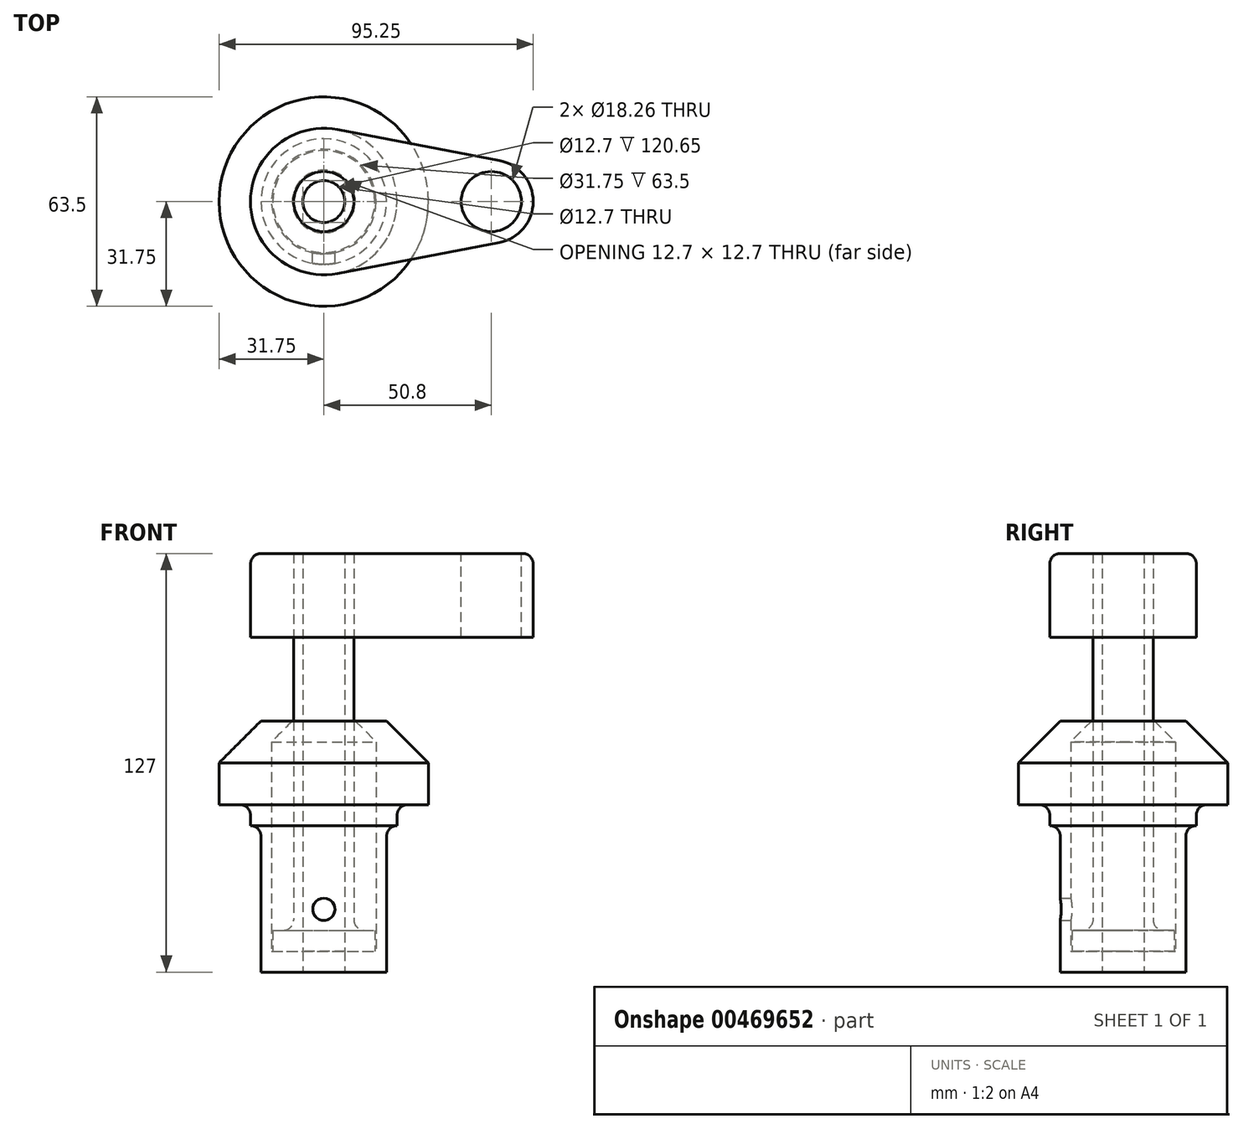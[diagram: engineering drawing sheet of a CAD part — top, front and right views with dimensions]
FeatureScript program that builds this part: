
annotation { "Feature Type Name" : "Feature", "Feature Type Description" : "" }
export const myFeature = defineFeature(function(context is Context, id is Id, definition is map)
    precondition{}
    {
        {
            var Q0;
            Q0=qCreatedBy(makeId("Front.planeOp"),FACE);
            var sketch = newSketch(context, id + "F0", { "sketchPlane" : qUnion([Q0])});
            skLineSegment(sketch, "E0", {"start": v(0, 0) * mm, "end": v(0, 76.2) * mm});
            skLineSegment(sketch, "E1", {"start": v(0, 76.2) * mm, "end": v(19.05, 76.2) * mm});
            skLineSegment(sketch, "E2", {"start": v(19.05, 76.2) * mm, "end": v(31.75, 63.5) * mm});
            skLineSegment(sketch, "E3", {"start": v(31.75, 63.5) * mm, "end": v(31.75, 50.8) * mm});
            skLineSegment(sketch, "E4", {"start": v(31.75, 50.8) * mm, "end": v(22.23, 50.8) * mm});
            skLineSegment(sketch, "E5", {"start": v(22.23, 50.8) * mm, "end": v(22.23, 44.45) * mm});
            skLineSegment(sketch, "E6", {"start": v(22.23, 44.45) * mm, "end": v(19.05, 44.45) * mm});
            skLineSegment(sketch, "E7", {"start": v(19.05, 44.45) * mm, "end": v(19.05, 0) * mm});
            skLineSegment(sketch, "E8", {"start": v(19.05, 0) * mm, "end": v(0, 0) * mm});
            skLineSegment(sketch, "E9", {"start": v(9.52, 76.2) * mm, "end": v(15.88, 69.85) * mm});
            skLineSegment(sketch, "E10", {"start": v(15.88, 69.85) * mm, "end": v(15.88, 6.35) * mm});
            skLineSegment(sketch, "E11", {"start": v(15.88, 6.35) * mm, "end": v(0, 6.35) * mm});
            skLineSegment(sketch, "E12", {"start": v(0, 76.2) * mm, "end": v(0, 90.67) * mm, "construction": true});
            skLineSegment(sketch, "E13", {"start": v(0, 76.2) * mm, "end": v(0, 127) * mm});
            skLineSegment(sketch, "E14", {"start": v(0, 127) * mm, "end": v(9.13, 127) * mm});
            skLineSegment(sketch, "E15", {"start": v(9.13, 127) * mm, "end": v(9.13, 12.7) * mm});
            skLineSegment(sketch, "E16", {"start": v(9.13, 12.7) * mm, "end": v(15.48, 12.7) * mm});
            skLineSegment(sketch, "E17", {"start": v(15.48, 12.7) * mm, "end": v(15.48, 6.35) * mm});
            skSolve(sketch);
        }
        {
            var Q0;
            {var subQ4=sQuery(id+"F0.wireOp",EDGE,"E2");Q0=makeQuery(id+"F0.imprint","IMPRINT",FACE,{"disambiguationData":[TD([[makeQuery(id+"F0.imprint","IMPRINT",EDGE,{"derivedFrom":subQ4}),-1.0]])]});}
            var Q1;
            Q1=sQuery(id+"F0.wireOp",EDGE,"E0");
            revolve(context, id + "F1", {"entities" : qUnion([Q0]), "axis" : qUnion([Q1]), "revolveType" : RevolveType.FULL});
        }
        {
            var Q0;
            {var subQ0=sQuery(id+"F0.wireOp",EDGE,"E13");Q0=makeQuery(id+"F0.imprint","IMPRINT",FACE,{"disambiguationData":[TD([[makeQuery(id+"F0.imprint","IMPRINT",EDGE,{"derivedFrom":subQ0}),-1.0]])]});}
            var Q1;
            {var subQ0=sQuery(id+"F0.wireOp",EDGE,"E16");Q1=makeQuery(id+"F0.imprint","IMPRINT",FACE,{"disambiguationData":[TD([[makeQuery(id+"F0.imprint","IMPRINT",EDGE,{"derivedFrom":subQ0}),-1.0]])]});}
            var Q2;
            Q2=sQuery(id+"F0.wireOp",EDGE,"E13");
            revolve(context, id + "F2", {"entities" : qUnion([Q0, Q1]), "axis" : qUnion([Q2]), "revolveType" : RevolveType.FULL});
        }
        {
            var Q0;
            Q0=makeQuery(id+"F2.opRevolve","SWEPT_FACE",FACE,{"disambiguationData":[OSD([sQuery(id+"F0.wireOp",EDGE,"E14")])]});
            var sketch = newSketch(context, id + "F3", { "sketchPlane" : qUnion([Q0])});
            skCircle(sketch, "E18", {"center": v(0, 0) * mm, "radius": 22.23 * mm});
            skCircle(sketch, "E19", {"center": v(50.8, 0) * mm, "radius": 12.7 * mm});
            skLineSegment(sketch, "E20", {"start": v(4.17, 21.83) * mm, "end": v(53.18, 12.47) * mm});
            skLineSegment(sketch, "E21", {"start": v(53.18, -12.47) * mm, "end": v(4.17, -21.83) * mm});
            skCircle(sketch, "E22.0", {"center": v(0, 0) * mm, "radius": 9.13 * mm});
            skCircle(sketch, "E23", {"center": v(50.8, 0) * mm, "radius": 9.13 * mm});
            skSolve(sketch);
        }
        {
            var Q0;
            Q0 = qSketchRegion(id + "F3", true);
            var Q1;
            Q1=makeQuery(id+"F1.opRevolve","SWEPT_FACE",FACE,{"disambiguationData":[OSD([sQuery(id+"F0.wireOp",EDGE,"E1")])]});
            extrude(context, id + "F4", {"entities" : qUnion([Q0]), "oppositeDirection" : true, "endBoundEntityFace" : qUnion([Q1]), "depth" : 25.4 * mm});
        }
        {
            var Q0;
            Q0=qCreatedBy(makeId("Front.planeOp"),FACE);
            var sketch = newSketch(context, id + "F5", { "sketchPlane" : qUnion([Q0])});
            skPoint(sketch, "E24", {"position": v(0, 19.05) * mm});
            skSolve(sketch);
        }
        {
            var Q0;
            Q0=sQuery(id+"F5.wireOp",VERTEX,"E24");
            var Q1;
            Q1=makeQuery(id+"F1.opRevolve","SWEPT_BODY",BODY,{"disambiguationData":[OSD([sQuery(id+"F0.wireOp",EDGE,"E0"),sQuery(id+"F0.wireOp",EDGE,"E1"),sQuery(id+"F0.wireOp",EDGE,"E2"),sQuery(id+"F0.wireOp",EDGE,"E3"),sQuery(id+"F0.wireOp",EDGE,"E4"),sQuery(id+"F0.wireOp",EDGE,"E5"),sQuery(id+"F0.wireOp",EDGE,"E6"),sQuery(id+"F0.wireOp",EDGE,"E7"),sQuery(id+"F0.wireOp",EDGE,"E8"),sQuery(id+"F0.wireOp",EDGE,"E9"),sQuery(id+"F0.wireOp",EDGE,"E10"),sQuery(id+"F0.wireOp",EDGE,"E11")])]});
            hole(context, id + "F6", {"style" : HoleStyle.SIMPLE, "endStyle" : HoleEndStyle.THROUGH, "oppositeDirection" : true, "standardTappedOrClearance" : lookupTablePath({ "standard" : "ANSI", "fit" : "Normal (ASME)", "size" : "1/4", "type" : "Clearance" }), "standardBlindInLast" : lookupTablePath({ "fit" : "Free", "standard" : "ANSI", "size" : "1/4", "type" : "Clearance" }), "holeDiameter" : 6.76 * mm, "tappedDepth" : 14.3 * mm, "tapClearance" : 3, "locations" : qUnion([Q0]), "scope" : qUnion([Q1])});
        }
        {
            var Q0;
            Q0=makeQuery(id+"F4.opExtrude","CAP_EDGE",EDGE,{"disambiguationData":[OSD([sQuery(id+"F3.wireOp",EDGE,"E20")])],"isStart":true});
            var Q1;
            Q1=makeQuery(id+"F1.opRevolve","SWEPT_EDGE",EDGE,{"disambiguationData":[OSD([sQuery(id+"F0.wireOp",EDGE,"E4"),sQuery(id+"F0.wireOp",EDGE,"E5")])]});
            var Q2;
            Q2=makeQuery(id+"F1.opRevolve","SWEPT_EDGE",EDGE,{"disambiguationData":[OSD([sQuery(id+"F0.wireOp",EDGE,"E6"),sQuery(id+"F0.wireOp",EDGE,"E7")])]});
            var Q3;
            Q3=makeQuery(id+"F2.opRevolve","SWEPT_EDGE",EDGE,{"disambiguationData":[OSD([sQuery(id+"F0.wireOp",EDGE,"E15"),sQuery(id+"F0.wireOp",EDGE,"E16")])]});
            fillet(context, id + "F7", {"entities" : qUnion([Q0, Q1, Q2, Q3]), "radius" : 3.17 * mm, "tangentPropagation" : true, "allowEdgeOverflow" : false});
        }
        {
            var Q0;
            Q0=makeQuery(id+"F1.opRevolve","SWEPT_FACE",FACE,{"disambiguationData":[OSD([sQuery(id+"F0.wireOp",EDGE,"E8")])]});
            var sketch = newSketch(context, id + "F8", { "sketchPlane" : qUnion([Q0])});
            skCircle(sketch, "E25", {"center": v(0, 0) * mm, "radius": 6.35 * mm});
            skSolve(sketch);
        }
        {
            var Q0;
            Q0 = qSketchRegion(id + "F8", true);
            extrude(context, id + "F9", {"entities" : qUnion([Q0]), "operationType" : NewBodyOperationType.REMOVE, "endBound" : BoundingType.THROUGH_ALL, "oppositeDirection" : true, "depth" : 25.4 * mm});
        }
    });
